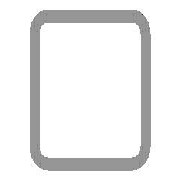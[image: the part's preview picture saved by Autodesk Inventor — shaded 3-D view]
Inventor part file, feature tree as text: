
AUTODESK INVENTOR PART (.ipt)
format: ipt  version: 2025.1 (Build 291241020, 241B)  size: 135,680 bytes
history: native  units: mm (DEFAULTED — no unit token found)
features: other x4, sketch x1, plane x1
ambient origin geometry x8: Origin, YZ Plane, XZ Plane, XY Plane, X Axis, Y Axis, Z Axis, Center Point
bodies: Solid1 (feature_tree), Body (feature_tree)
feature tree (6):
  parser-record x1  (decoder bookkeeping rows leaked as tree rows — omitted from the tree; the rows remain in map.json)
  other  "Driven Length"
  other  "Start plane"
  other  "End plane"
  sketch  "Sketch3"  dims[d3=7000.0mm d4=0.0mm d7=8.0mm d9=100.0mm d11=100.0mm d12=4.0mm d13=-0.0mm d14=7000.0mm d15=50.0mm d16=50.0mm d17=90.0deg d18=7000.0mm]
  plane  "Work Plane3"
